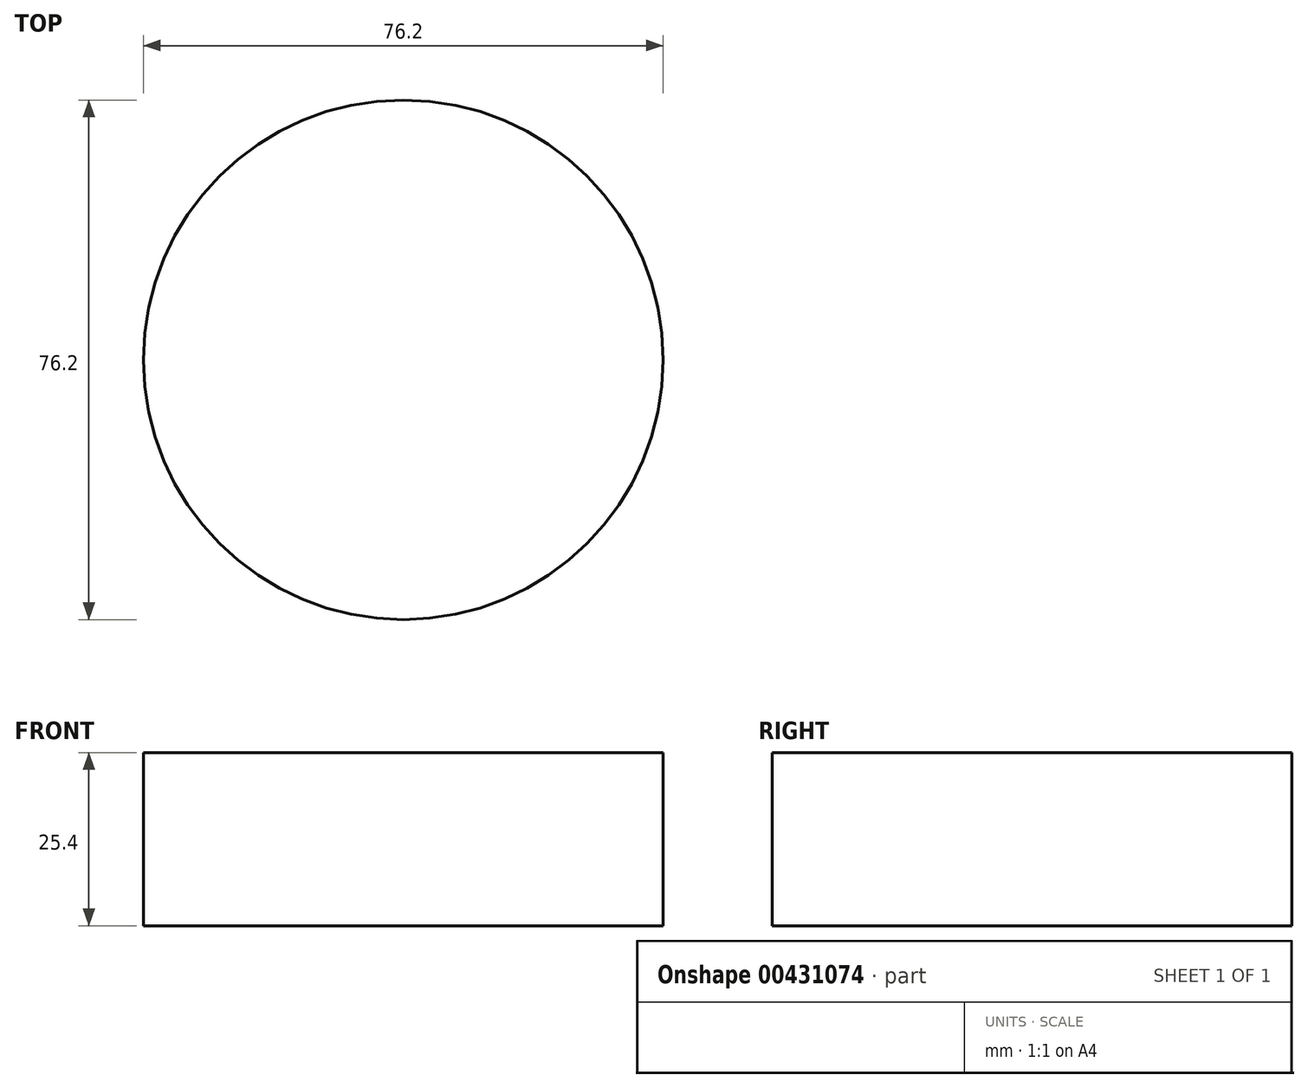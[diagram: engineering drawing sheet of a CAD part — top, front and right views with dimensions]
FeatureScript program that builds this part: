
annotation { "Feature Type Name" : "Feature", "Feature Type Description" : "" }
export const myFeature = defineFeature(function(context is Context, id is Id, definition is map)
    precondition{}
    {
        {
            var Q0;
            Q0=qCreatedBy(makeId("Top.planeOp"),FACE);
            var sketch = newSketch(context, id + "F0", { "sketchPlane" : qUnion([Q0])});
            skCircle(sketch, "E0", {"center": v(0, 0) * mm, "radius": 38.1 * mm});
            skLineSegment(sketch, "E1.left", {"start": v(8.69, -12.85) * mm, "end": v(8.69, -12.85) * mm});
            skLineSegment(sketch, "E1.right", {"start": v(-8.69, -12.85) * mm, "end": v(-8.69, 12.85) * mm});
            skArc(sketch, "E2", {"start": v(-11.23, -12.85) * mm, "mid": v(-1.27, -15.9) * mm, "end": v(8.69, -12.85) * mm});
            skArc(sketch, "E3", {"start": v(8.69, 16.6) * mm, "mid": v(-1.27, 19.66) * mm, "end": v(-11.23, 16.6) * mm});
            skLineSegment(sketch, "E4", {"start": v(8.69, -12.85) * mm, "end": v(8.69, 12.85) * mm});
            skSolve(sketch);
        }
        {
            var Q0;
            Q0 = qSketchRegion(id + "F0", true);
            extrude(context, id + "F1", {"entities" : qUnion([Q0]), "depth" : 25.4 * mm});
        }
    });
